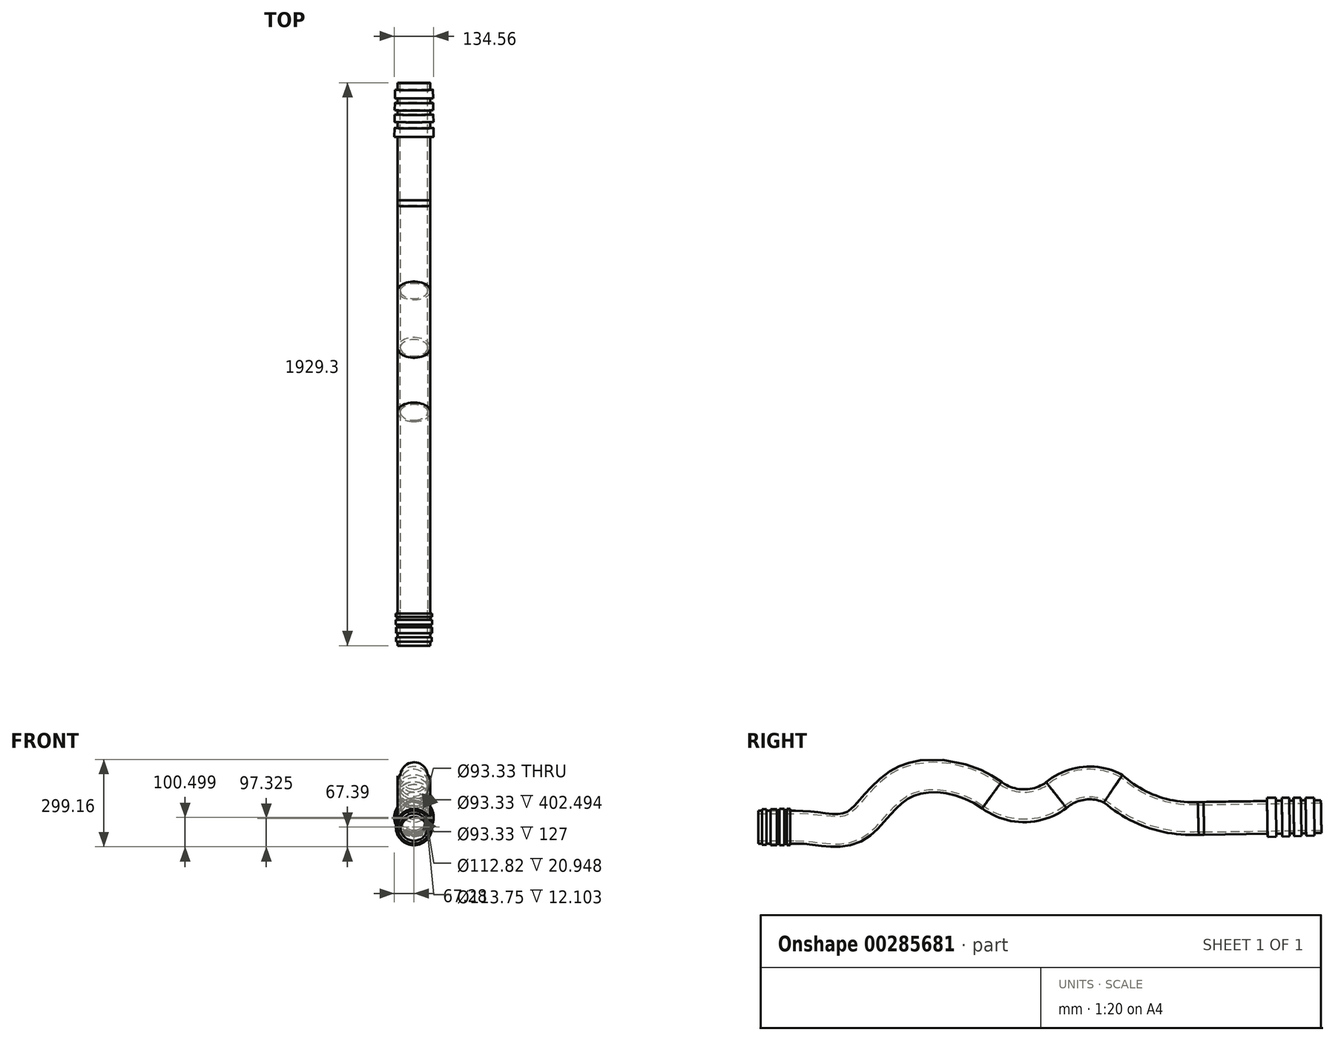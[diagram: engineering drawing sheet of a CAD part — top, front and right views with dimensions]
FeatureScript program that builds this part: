
annotation { "Feature Type Name" : "Feature", "Feature Type Description" : "" }
export const myFeature = defineFeature(function(context is Context, id is Id, definition is map)
    precondition{}
    {
        {
            var Q0;
            Q0=qCreatedBy(makeId("Front.planeOp"),FACE);
            var sketch = newSketch(context, id + "F0", { "sketchPlane" : qUnion([Q0])});
            skCircle(sketch, "E0", {"center": v(0, 0) * mm, "radius": 56.15 * mm});
            skCircle(sketch, "E1", {"center": v(0, 0) * mm, "radius": 46.66 * mm});
            skSolve(sketch);
        }
        {
            var Q0;
            Q0=qCreatedBy(makeId("Right.planeOp"),FACE);
            var sketch = newSketch(context, id + "F1", { "sketchPlane" : qUnion([Q0])});
            skFitSpline(sketch, "E2", {"points": [v(0, 0) * mm, v(198.37, 0) * mm, v(363.75, 149.52) * mm, v(673.12, 109.6) * mm], "startDerivative": vector(781.62, 0) * mm, "endDerivative": vector(768.64, -553.87) * mm});
            skArc(sketch, "E3", {"start": v(673.12, 109.6) * mm, "mid": v(783.6, 73.23) * mm, "end": v(894.1, 109.6) * mm});
            skArc(sketch, "E4", {"start": v(1088.79, 131.92) * mm, "mid": v(988.06, 150.28) * mm, "end": v(894.1, 109.6) * mm});
            skArc(sketch, "E5", {"start": v(1088.79, 131.92) * mm, "mid": v(1224.45, 52.08) * mm, "end": v(1380.3, 29.94) * mm});
            skLineSegment(sketch, "E6", {"start": v(1399.34, 29.94) * mm, "end": v(1801.41, 36.28) * mm});
            skLineSegment(sketch, "E7", {"start": v(1399.34, 29.94) * mm, "end": v(1380.3, 29.94) * mm});
            skSolve(sketch);
        }
        {
            var Q0;
            Q0=makeQuery(id+"F0.imprint","IMPRINT",FACE,{"disambiguationData":[TD([[makeQuery(id+"F0.imprint","IMPRINT",EDGE,{"derivedFrom":sQuery(id+"F0.wireOp",EDGE,"E0")}),1.0]])]});
            var Q1;
            Q1=sQuery(id+"F1.wireOp",EDGE,"E2");
            var Q2;
            Q2=sQuery(id+"F1.wireOp",EDGE,"E3");
            var Q3;
            Q3=sQuery(id+"F1.wireOp",EDGE,"E4");
            var Q4;
            Q4=sQuery(id+"F1.wireOp",EDGE,"E5");
            var Q5;
            Q5=sQuery(id+"F1.wireOp",EDGE,"E6");
            var Q6;
            Q6=sQuery(id+"F1.wireOp",EDGE,"E7");
            sweep(context, id + "F2", {"profiles" : qUnion([Q0]), "path" : qUnion([Q1, Q2, Q3, Q4, Q5, Q6])});
        }
        {
            var Q0;
            Q0=makeQuery(id+"F2.opSweep","CAP_FACE",FACE,{"disambiguationData":[OSD([sQuery(id+"F0.wireOp",EDGE,"E0"),sQuery(id+"F0.wireOp",EDGE,"E1"),sQuery(id+"F1.wireOp",VERTEX,"E2.start")])],"isStart":true});
            extrude(context, id + "F3", {"entities" : qUnion([Q0]), "operationType" : NewBodyOperationType.ADD, "depth" : 127 * mm});
        }
        {
            var Q0;
            Q0=qCreatedBy(makeId("Top.planeOp"),FACE);
            var sketch = newSketch(context, id + "F4", { "sketchPlane" : qUnion([Q0])});
            skLineSegment(sketch, "E8.bottom", {"start": v(-55.48, -113.62) * mm, "end": v(-61.06, -113.62) * mm});
            skLineSegment(sketch, "E8.top", {"start": v(-55.48, -98.25) * mm, "end": v(-61.06, -98.25) * mm});
            skLineSegment(sketch, "E8.left", {"start": v(-55.48, -113.62) * mm, "end": v(-55.48, -98.25) * mm});
            skLineSegment(sketch, "E8.right", {"start": v(-61.06, -113.62) * mm, "end": v(-61.06, -98.25) * mm});
            skLineSegment(sketch, "E9.bottom", {"start": v(-56.4, -84.29) * mm, "end": v(-61.53, -84.29) * mm});
            skLineSegment(sketch, "E9.top", {"start": v(-56.4, -63.34) * mm, "end": v(-61.53, -63.34) * mm});
            skLineSegment(sketch, "E9.left", {"start": v(-56.4, -84.29) * mm, "end": v(-56.4, -63.34) * mm});
            skLineSegment(sketch, "E9.right", {"start": v(-61.53, -84.29) * mm, "end": v(-61.53, -63.34) * mm});
            skLineSegment(sketch, "E10.bottom", {"start": v(-55.94, -54.5) * mm, "end": v(-62, -54.5) * mm});
            skLineSegment(sketch, "E10.top", {"start": v(-55.94, -38.2) * mm, "end": v(-62, -38.2) * mm});
            skLineSegment(sketch, "E10.left", {"start": v(-55.94, -54.5) * mm, "end": v(-55.94, -38.2) * mm});
            skLineSegment(sketch, "E10.right", {"start": v(-62, -54.5) * mm, "end": v(-62, -38.2) * mm});
            skLineSegment(sketch, "E11.bottom", {"start": v(-56.87, -28.9) * mm, "end": v(-62, -28.9) * mm});
            skLineSegment(sketch, "E11.top", {"start": v(-56.87, -16.79) * mm, "end": v(-62, -16.79) * mm});
            skLineSegment(sketch, "E11.left", {"start": v(-56.87, -28.9) * mm, "end": v(-56.87, -16.79) * mm});
            skLineSegment(sketch, "E11.right", {"start": v(-62, -28.9) * mm, "end": v(-62, -16.79) * mm});
            skSolve(sketch);
        }
        {
            var Q0;
            Q0=makeQuery(id+"F4.imprint","IMPRINT",FACE,{"disambiguationData":[TD([[makeQuery(id+"F4.imprint","IMPRINT",EDGE,{"derivedFrom":sQuery(id+"F4.wireOp",EDGE,"E8.bottom")}),-1.0]])]});
            var Q1;
            Q1=makeQuery(id+"F4.imprint","IMPRINT",FACE,{"disambiguationData":[TD([[makeQuery(id+"F4.imprint","IMPRINT",EDGE,{"derivedFrom":sQuery(id+"F4.wireOp",EDGE,"E9.bottom")}),-1.0]])]});
            var Q2;
            Q2=makeQuery(id+"F4.imprint","IMPRINT",FACE,{"disambiguationData":[TD([[makeQuery(id+"F4.imprint","IMPRINT",EDGE,{"derivedFrom":sQuery(id+"F4.wireOp",EDGE,"E10.bottom")}),-1.0]])]});
            var Q3;
            Q3=makeQuery(id+"F4.imprint","IMPRINT",FACE,{"disambiguationData":[TD([[makeQuery(id+"F4.imprint","IMPRINT",EDGE,{"derivedFrom":sQuery(id+"F4.wireOp",EDGE,"E11.bottom")}),-1.0]])]});
            var Q4;
            Q4=makeQuery(id+"F3.opExtrude","CAP_EDGE",EDGE,{"disambiguationData":[OSD([sQuery(id+"F0.wireOp",EDGE,"E1"),sQuery(id+"F1.wireOp",VERTEX,"E2.start")])],"isStart":false});
            revolve(context, id + "F5", {"operationType" : NewBodyOperationType.ADD, "entities" : qUnion([Q0, Q1, Q2, Q3]), "axis" : qUnion([Q4]), "revolveType" : RevolveType.FULL});
        }
        {
            var Q0;
            Q0=qCreatedBy(makeId("Right.planeOp"),FACE);
            var sketch = newSketch(context, id + "F6", { "sketchPlane" : qUnion([Q0])});
            skLineSegment(sketch, "E12.bottom", {"start": v(1776.66, 90.31) * mm, "end": v(1747.96, 90.31) * mm});
            skLineSegment(sketch, "E12.top", {"start": v(1776.66, 100.64) * mm, "end": v(1747.96, 100.64) * mm});
            skLineSegment(sketch, "E12.left", {"start": v(1776.66, 90.31) * mm, "end": v(1776.66, 100.64) * mm});
            skLineSegment(sketch, "E12.right", {"start": v(1747.96, 90.31) * mm, "end": v(1747.96, 100.64) * mm});
            skLineSegment(sketch, "E13.bottom", {"start": v(1731.89, 86.87) * mm, "end": v(1706.63, 86.87) * mm});
            skLineSegment(sketch, "E13.top", {"start": v(1731.89, 100.64) * mm, "end": v(1706.63, 100.64) * mm});
            skLineSegment(sketch, "E13.left", {"start": v(1731.89, 86.87) * mm, "end": v(1731.89, 100.64) * mm});
            skLineSegment(sketch, "E13.right", {"start": v(1706.63, 86.87) * mm, "end": v(1706.63, 100.64) * mm});
            skLineSegment(sketch, "E14.bottom", {"start": v(1691.71, 90.31) * mm, "end": v(1666.46, 90.31) * mm});
            skLineSegment(sketch, "E14.top", {"start": v(1691.71, 100.64) * mm, "end": v(1666.46, 100.64) * mm});
            skLineSegment(sketch, "E14.left", {"start": v(1691.71, 90.31) * mm, "end": v(1691.71, 100.64) * mm});
            skLineSegment(sketch, "E14.right", {"start": v(1666.46, 90.31) * mm, "end": v(1666.46, 100.64) * mm});
            skLineSegment(sketch, "E15.bottom", {"start": v(1645.8, 88.01) * mm, "end": v(1615.95, 88.01) * mm});
            skLineSegment(sketch, "E15.top", {"start": v(1645.8, 100.64) * mm, "end": v(1615.95, 100.64) * mm});
            skLineSegment(sketch, "E15.left", {"start": v(1645.8, 88.01) * mm, "end": v(1645.8, 100.64) * mm});
            skLineSegment(sketch, "E15.right", {"start": v(1615.95, 88.01) * mm, "end": v(1615.95, 100.64) * mm});
            skSolve(sketch);
        }
        {
            var Q0;
            Q0=makeQuery(id+"F6.imprint","IMPRINT",FACE,{"disambiguationData":[TD([[makeQuery(id+"F6.imprint","IMPRINT",EDGE,{"derivedFrom":sQuery(id+"F6.wireOp",EDGE,"E12.bottom")}),-1.0]])]});
            var Q1;
            Q1=makeQuery(id+"F6.imprint","IMPRINT",FACE,{"disambiguationData":[TD([[makeQuery(id+"F6.imprint","IMPRINT",EDGE,{"derivedFrom":sQuery(id+"F6.wireOp",EDGE,"E13.bottom")}),-1.0]])]});
            var Q2;
            Q2=makeQuery(id+"F6.imprint","IMPRINT",FACE,{"disambiguationData":[TD([[makeQuery(id+"F6.imprint","IMPRINT",EDGE,{"derivedFrom":sQuery(id+"F6.wireOp",EDGE,"E14.bottom")}),-1.0]])]});
            var Q3;
            Q3=makeQuery(id+"F6.imprint","IMPRINT",FACE,{"disambiguationData":[TD([[makeQuery(id+"F6.imprint","IMPRINT",EDGE,{"derivedFrom":sQuery(id+"F6.wireOp",EDGE,"E15.bottom")}),-1.0]])]});
            var Q4;
            Q4=makeQuery(id+"F2.opSweep","CAP_EDGE",EDGE,{"disambiguationData":[OSD([sQuery(id+"F0.wireOp",EDGE,"E1"),sQuery(id+"F1.wireOp",VERTEX,"E6.end")])],"isStart":false});
            revolve(context, id + "F7", {"operationType" : NewBodyOperationType.ADD, "entities" : qUnion([Q0, Q1, Q2, Q3]), "axis" : qUnion([Q4]), "revolveType" : RevolveType.FULL});
        }
    });
